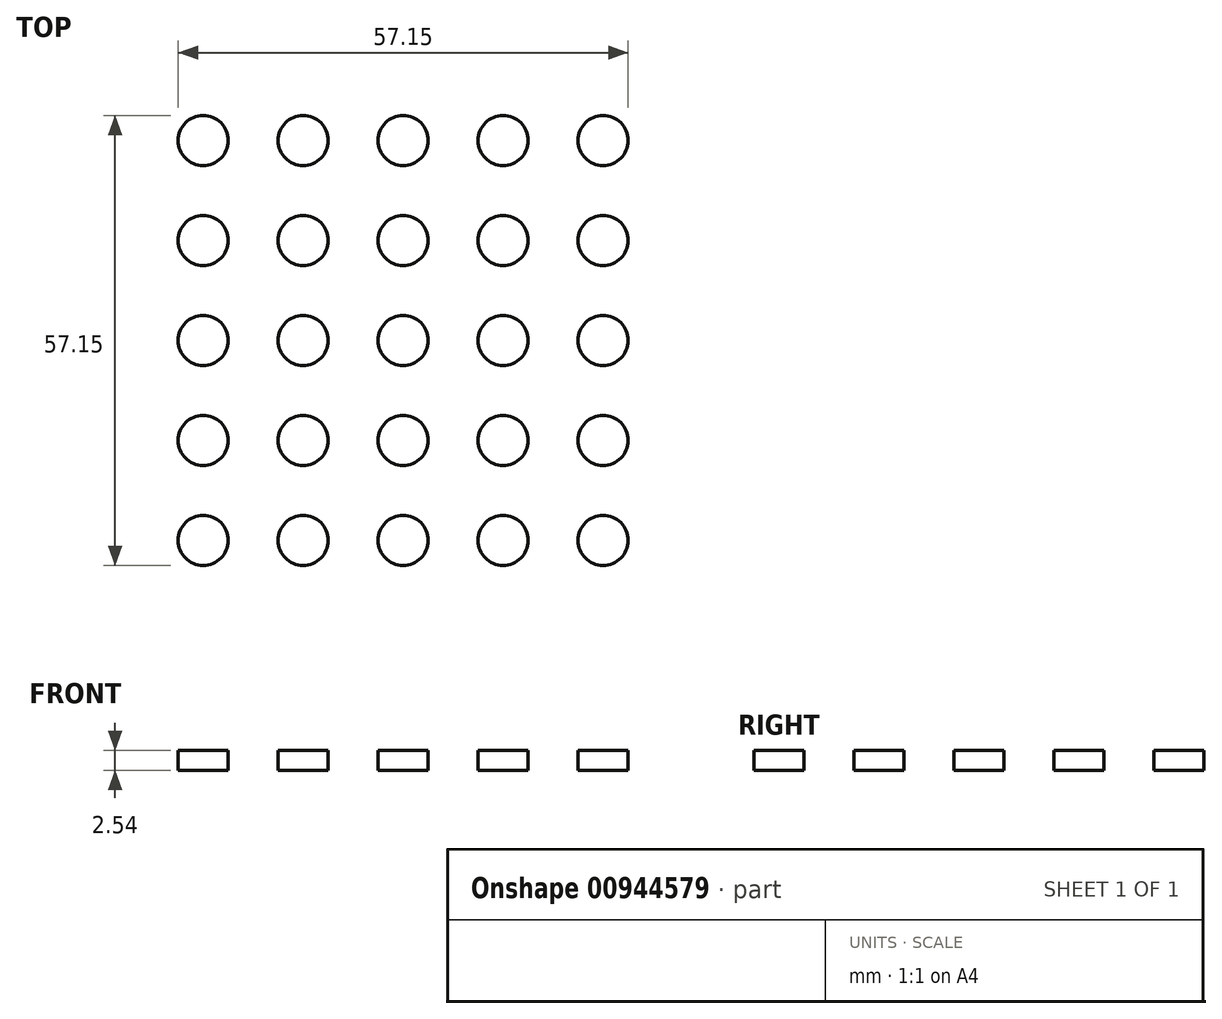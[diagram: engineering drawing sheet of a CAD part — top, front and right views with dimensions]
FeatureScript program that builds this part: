
annotation { "Feature Type Name" : "Feature", "Feature Type Description" : "" }
export const myFeature = defineFeature(function(context is Context, id is Id, definition is map)
    precondition{}
    {
        {
            var Q0;
            Q0=qCreatedBy(makeId("Top.planeOp"),FACE);
            var sketch = newSketch(context, id + "F0", { "sketchPlane" : qUnion([Q0])});
            skCircle(sketch, "E0", {"center": v(-59.64, -43.16) * mm, "radius": 3.18 * mm});
            skCircle(sketch, "E1.0.1.0", {"center": v(-59.64, -30.46) * mm, "radius": 3.18 * mm});
            skCircle(sketch, "E1.0.2.0", {"center": v(-59.64, -17.76) * mm, "radius": 3.18 * mm});
            skCircle(sketch, "E1.0.3.0", {"center": v(-59.64, -5.06) * mm, "radius": 3.18 * mm});
            skCircle(sketch, "E1.0.4.0", {"center": v(-59.64, 7.64) * mm, "radius": 3.18 * mm});
            skCircle(sketch, "E1.1.0.0", {"center": v(-46.94, -43.16) * mm, "radius": 3.18 * mm});
            skCircle(sketch, "E1.1.1.0", {"center": v(-46.94, -30.46) * mm, "radius": 3.18 * mm});
            skCircle(sketch, "E1.1.2.0", {"center": v(-46.94, -17.76) * mm, "radius": 3.18 * mm});
            skCircle(sketch, "E1.1.3.0", {"center": v(-46.94, -5.06) * mm, "radius": 3.18 * mm});
            skCircle(sketch, "E1.1.4.0", {"center": v(-46.94, 7.64) * mm, "radius": 3.18 * mm});
            skCircle(sketch, "E1.2.0.0", {"center": v(-34.24, -43.16) * mm, "radius": 3.18 * mm});
            skCircle(sketch, "E1.2.1.0", {"center": v(-34.24, -30.46) * mm, "radius": 3.18 * mm});
            skCircle(sketch, "E1.2.2.0", {"center": v(-34.24, -17.76) * mm, "radius": 3.18 * mm});
            skCircle(sketch, "E1.2.3.0", {"center": v(-34.24, -5.06) * mm, "radius": 3.18 * mm});
            skCircle(sketch, "E1.2.4.0", {"center": v(-34.24, 7.64) * mm, "radius": 3.18 * mm});
            skCircle(sketch, "E1.3.0.0", {"center": v(-21.54, -43.16) * mm, "radius": 3.18 * mm});
            skCircle(sketch, "E1.3.1.0", {"center": v(-21.54, -30.46) * mm, "radius": 3.18 * mm});
            skCircle(sketch, "E1.3.2.0", {"center": v(-21.54, -17.76) * mm, "radius": 3.18 * mm});
            skCircle(sketch, "E1.3.3.0", {"center": v(-21.54, -5.06) * mm, "radius": 3.18 * mm});
            skCircle(sketch, "E1.3.4.0", {"center": v(-21.54, 7.64) * mm, "radius": 3.18 * mm});
            skCircle(sketch, "E1.4.0.0", {"center": v(-8.84, -43.16) * mm, "radius": 3.18 * mm});
            skCircle(sketch, "E1.4.1.0", {"center": v(-8.84, -30.46) * mm, "radius": 3.18 * mm});
            skCircle(sketch, "E1.4.2.0", {"center": v(-8.84, -17.76) * mm, "radius": 3.18 * mm});
            skCircle(sketch, "E1.4.3.0", {"center": v(-8.84, -5.06) * mm, "radius": 3.18 * mm});
            skCircle(sketch, "E1.4.4.0", {"center": v(-8.84, 7.64) * mm, "radius": 3.18 * mm});
            skLineSegment(sketch, "E1.direction1", {"start": v(-59.64, -43.16) * mm, "end": v(-46.94, -43.16) * mm, "construction": true});
            skLineSegment(sketch, "E1.direction2", {"start": v(-59.64, -43.16) * mm, "end": v(-59.64, -30.46) * mm, "construction": true});
            skSolve(sketch);
        }
        {
            var Q0;
            Q0 = qSketchRegion(id + "F0", true);
            extrude(context, id + "F1", {"entities" : qUnion([Q0]), "depth" : 2.54 * mm, "offsetDistance" : 25.4 * mm});
        }
    });
